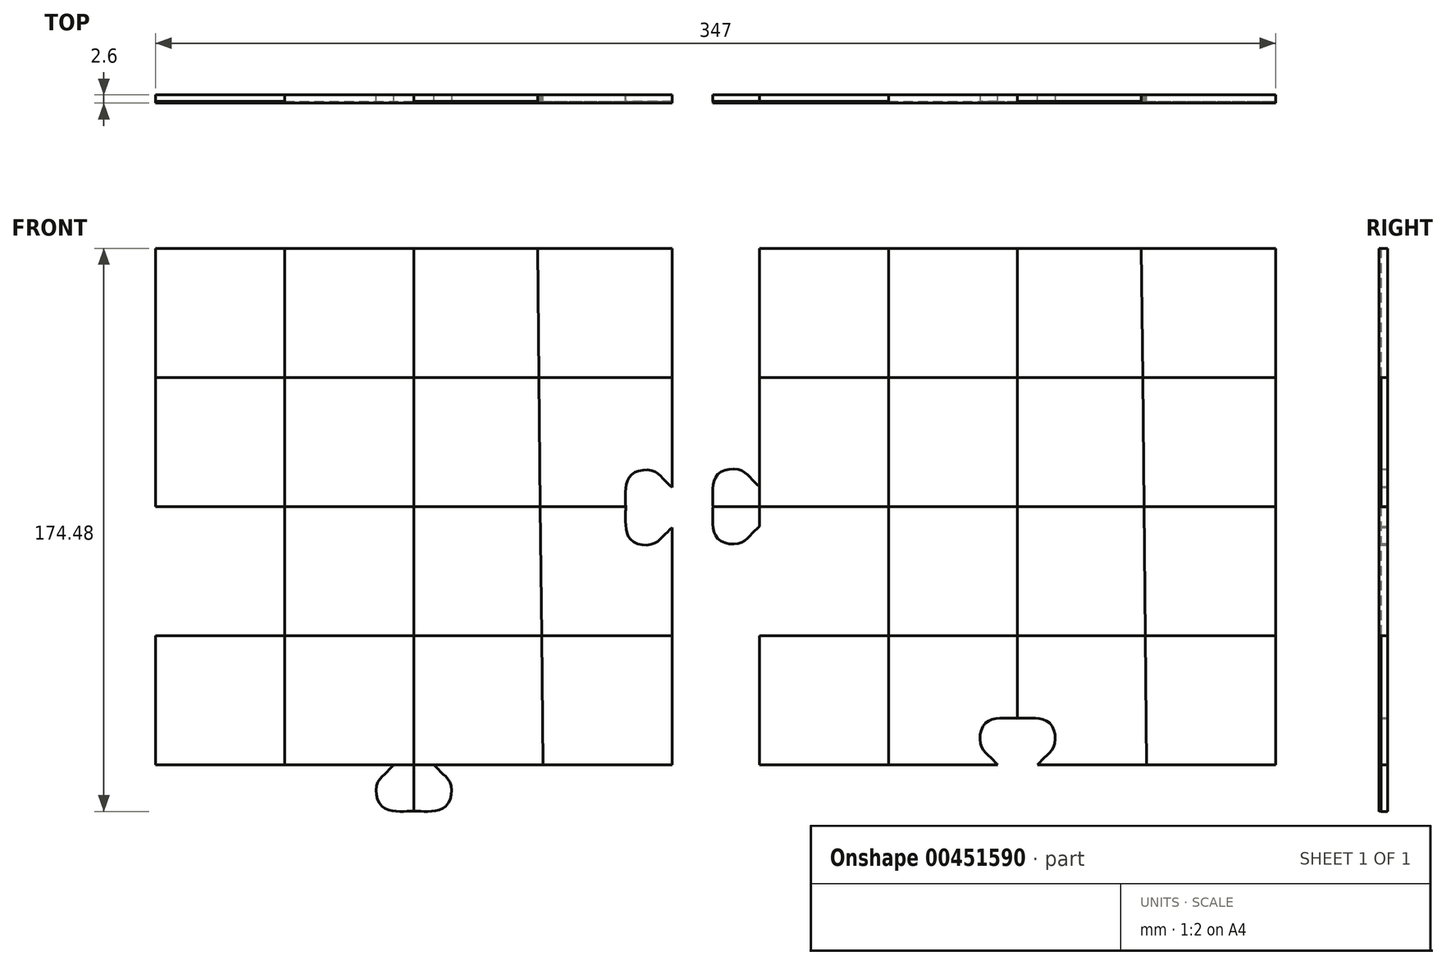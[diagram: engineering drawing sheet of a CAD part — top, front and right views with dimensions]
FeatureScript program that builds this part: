
annotation { "Feature Type Name" : "Feature", "Feature Type Description" : "" }
export const myFeature = defineFeature(function(context is Context, id is Id, definition is map)
    precondition{}
    {
        {
            var Q0;
            Q0=qCreatedBy(makeId("Front.planeOp"),FACE);
            var sketch = newSketch(context, id + "F0", { "sketchPlane" : qUnion([Q0])});
            skLineSegment(sketch, "E0.bottom", {"start": v(-114.43, 88.84) * mm, "end": v(45.57, 88.84) * mm});
            skLineSegment(sketch, "E0.top", {"start": v(-114.43, -71.16) * mm, "end": v(45.57, -71.16) * mm});
            skLineSegment(sketch, "E0.left", {"start": v(-114.43, 88.84) * mm, "end": v(-114.43, -71.16) * mm});
            skLineSegment(sketch, "E0.right", {"start": v(45.57, 88.84) * mm, "end": v(45.57, -71.16) * mm});
            skLineSegment(sketch, "E1", {"start": v(-34.43, 88.84) * mm, "end": v(-34.43, -71.16) * mm});
            skLineSegment(sketch, "E2", {"start": v(-74.43, 88.84) * mm, "end": v(-74.43, -71.16) * mm});
            skLineSegment(sketch, "E3", {"start": v(3.9, 88.84) * mm, "end": v(5.57, -71.16) * mm});
            skLineSegment(sketch, "E4", {"start": v(-114.43, 8.84) * mm, "end": v(45.57, 8.84) * mm});
            skLineSegment(sketch, "E5", {"start": v(-114.43, 48.84) * mm, "end": v(45.57, 48.84) * mm});
            skLineSegment(sketch, "E6", {"start": v(-114.43, 8.84) * mm, "end": v(-114.43, -31.16) * mm});
            skLineSegment(sketch, "E7", {"start": v(-114.43, -31.16) * mm, "end": v(45.57, -31.16) * mm});
            skFitSpline(sketch, "E8", {"points": [v(-114.43, 2.66) * mm, v(-117.14, 0) * mm, v(-120.5, -2.53) * mm, v(-126.7, -1.62) * mm, v(-128.78, 2.84) * mm, v(-128.87, 7.11) * mm, v(-128.78, 8.84) * mm], "startDerivative": vector(-16.05, -15.15) * mm, "endDerivative": vector(1.61, 12.92) * mm});
            skFitSpline(sketch, "E9.MirrorCS", {"points": [v(-114.43, 15.03) * mm, v(-117.14, 17.69) * mm, v(-120.5, 20.22) * mm, v(-126.7, 19.3) * mm, v(-128.78, 14.85) * mm, v(-128.87, 10.57) * mm, v(-128.78, 8.84) * mm], "startDerivative": vector(-16.05, 15.15) * mm, "endDerivative": vector(1.61, -12.92) * mm});
            skLineSegment(sketch, "E10.bottom", {"start": v(-301.43, 88.84) * mm, "end": v(-141.43, 88.84) * mm});
            skLineSegment(sketch, "E10.top", {"start": v(-301.43, -71.16) * mm, "end": v(-141.43, -71.16) * mm});
            skLineSegment(sketch, "E10.left", {"start": v(-301.43, 88.84) * mm, "end": v(-301.43, -71.16) * mm});
            skLineSegment(sketch, "E10.right", {"start": v(-141.43, 88.84) * mm, "end": v(-141.43, -71.16) * mm});
            skLineSegment(sketch, "E11", {"start": v(-221.43, 88.84) * mm, "end": v(-221.43, -71.16) * mm});
            skLineSegment(sketch, "E12", {"start": v(-261.43, 88.84) * mm, "end": v(-261.43, -71.16) * mm});
            skLineSegment(sketch, "E13", {"start": v(-183.1, 88.84) * mm, "end": v(-181.43, -71.16) * mm});
            skLineSegment(sketch, "E14", {"start": v(-301.43, 8.84) * mm, "end": v(-141.43, 8.84) * mm});
            skLineSegment(sketch, "E15", {"start": v(-301.43, 48.84) * mm, "end": v(-141.43, 48.84) * mm});
            skLineSegment(sketch, "E16", {"start": v(-301.43, 8.84) * mm, "end": v(-301.43, -31.16) * mm});
            skLineSegment(sketch, "E17", {"start": v(-301.43, -31.16) * mm, "end": v(-141.43, -31.16) * mm});
            skFitSpline(sketch, "E18", {"points": [v(-141.43, 2.37) * mm, v(-144.14, -0.29) * mm, v(-147.5, -2.82) * mm, v(-153.7, -1.9) * mm, v(-155.78, 2.55) * mm, v(-155.87, 6.83) * mm, v(-155.78, 8.56) * mm], "startDerivative": vector(-16.05, -15.15) * mm, "endDerivative": vector(1.61, 12.92) * mm});
            skFitSpline(sketch, "E19.MirrorCS", {"points": [v(-141.43, 14.74) * mm, v(-144.14, 17.4) * mm, v(-147.5, 19.93) * mm, v(-153.7, 19.02) * mm, v(-155.78, 14.56) * mm, v(-155.87, 10.29) * mm, v(-155.78, 8.56) * mm], "startDerivative": vector(-16.05, 15.15) * mm, "endDerivative": vector(1.61, -12.92) * mm});
            skFitSpline(sketch, "E20.MirrorCS", {"points": [v(-227.62, -71.16) * mm, v(-230.27, -73.86) * mm, v(-232.8, -77.23) * mm, v(-231.9, -83.42) * mm, v(-227.44, -85.51) * mm, v(-223.16, -85.6) * mm, v(-221.43, -85.51) * mm], "startDerivative": vector(-15.15, -16.05) * mm, "endDerivative": vector(12.92, 1.61) * mm});
            skFitSpline(sketch, "E21.MirrorCS", {"points": [v(-215.24, -71.16) * mm, v(-212.59, -73.86) * mm, v(-210.05, -77.23) * mm, v(-210.96, -83.42) * mm, v(-215.42, -85.51) * mm, v(-219.7, -85.6) * mm, v(-221.43, -85.51) * mm], "startDerivative": vector(15.15, -16.05) * mm, "endDerivative": vector(-12.92, 1.61) * mm});
            skLineSegment(sketch, "E22", {"start": v(-114.43, 8.84) * mm, "end": v(-128.78, 8.84) * mm});
            skFitSpline(sketch, "E23.MirrorCS", {"points": [v(-28.24, -71.16) * mm, v(-25.59, -68.45) * mm, v(-23.05, -65.08) * mm, v(-23.96, -58.9) * mm, v(-28.42, -56.8) * mm, v(-32.7, -56.71) * mm, v(-34.43, -56.8) * mm], "startDerivative": vector(15.15, 16.05) * mm, "endDerivative": vector(-12.92, -1.61) * mm});
            skFitSpline(sketch, "E24.MirrorCS", {"points": [v(-40.62, -71.16) * mm, v(-43.27, -68.45) * mm, v(-45.8, -65.08) * mm, v(-44.9, -58.9) * mm, v(-40.44, -56.8) * mm, v(-36.16, -56.71) * mm, v(-34.43, -56.8) * mm], "startDerivative": vector(-15.15, 16.05) * mm, "endDerivative": vector(12.92, -1.61) * mm});
            skLineSegment(sketch, "E25", {"start": v(-221.43, -71.16) * mm, "end": v(-221.43, -85.51) * mm});
            skSolve(sketch);
        }
        {
            var Q0;
            {var subQ0=sQuery(id+"F0.wireOp",EDGE,"E0.left");var subQ1=sQuery(id+"F0.wireOp",EDGE,"E0.bottom");var subQ2=makeQuery(id+"F0.imprint","INTERSECT",VERTEX,{"derivedFrom":[subQ1,subQ0]});Q0=makeQuery(id+"F0.imprint","IMPRINT",FACE,{"disambiguationData":[TD([[makeQuery(id+"F0.imprint","IMPRINT",EDGE,{"disambiguationData":[TD([[subQ2,-1.0]])],"derivedFrom":subQ1}),-1.0]])]});}
            var Q1;
            {var subQ0=sQuery(id+"F0.wireOp",EDGE,"E1");var subQ1=sQuery(id+"F0.wireOp",EDGE,"E0.bottom");var subQ2=makeQuery(id+"F0.imprint","INTERSECT",VERTEX,{"derivedFrom":[subQ1,subQ0]});Q1=makeQuery(id+"F0.imprint","IMPRINT",FACE,{"disambiguationData":[TD([[makeQuery(id+"F0.imprint","IMPRINT",EDGE,{"disambiguationData":[TD([[subQ2,-1.0]])],"derivedFrom":subQ1}),-1.0]])]});}
            var Q2;
            {var subQ0=sQuery(id+"F0.wireOp",EDGE,"E5");var subQ1=sQuery(id+"F0.wireOp",EDGE,"E1");var subQ2=makeQuery(id+"F0.imprint","INTERSECT",VERTEX,{"derivedFrom":[subQ1,subQ0]});Q2=makeQuery(id+"F0.imprint","IMPRINT",FACE,{"disambiguationData":[TD([[makeQuery(id+"F0.imprint","IMPRINT",EDGE,{"disambiguationData":[TD([[subQ2,-1.0]])],"derivedFrom":subQ1}),-1.0]])]});}
            var Q3;
            {var subQ0=sQuery(id+"F0.wireOp",EDGE,"E4");var subQ1=sQuery(id+"F0.wireOp",EDGE,"E0.right");var subQ2=makeQuery(id+"F0.imprint","INTERSECT",VERTEX,{"derivedFrom":[subQ1,subQ0]});Q3=makeQuery(id+"F0.imprint","IMPRINT",FACE,{"disambiguationData":[TD([[makeQuery(id+"F0.imprint","IMPRINT",EDGE,{"disambiguationData":[TD([[subQ2,1.0]])],"derivedFrom":subQ1}),-1.0]])]});}
            var Q4;
            {var subQ5=sQuery(id+"F0.wireOp",EDGE,"E6");Q4=makeQuery(id+"F0.imprint","IMPRINT",FACE,{"disambiguationData":[TD([[makeQuery(id+"F0.imprint","IMPRINT",EDGE,{"derivedFrom":subQ5}),1.0]])]});}
            var Q5;
            {var subQ0=sQuery(id+"F0.wireOp",EDGE,"E4");var subQ1=sQuery(id+"F0.wireOp",EDGE,"E1");var subQ2=makeQuery(id+"F0.imprint","INTERSECT",VERTEX,{"derivedFrom":[subQ1,subQ0]});Q5=makeQuery(id+"F0.imprint","IMPRINT",FACE,{"disambiguationData":[TD([[makeQuery(id+"F0.imprint","IMPRINT",EDGE,{"disambiguationData":[TD([[subQ2,-1.0]])],"derivedFrom":subQ1}),1.0]])]});}
            var Q6;
            {var subQ0=sQuery(id+"F0.wireOp",EDGE,"E1");var subQ1=sQuery(id+"F0.wireOp",EDGE,"E0.top");var subQ2=makeQuery(id+"F0.imprint","INTERSECT",VERTEX,{"derivedFrom":[subQ1,subQ0]});Q6=makeQuery(id+"F0.imprint","IMPRINT",FACE,{"disambiguationData":[TD([[makeQuery(id+"F0.imprint","IMPRINT",EDGE,{"disambiguationData":[TD([[subQ2,1.0]])],"derivedFrom":subQ1}),1.0]])]});}
            var Q7;
            {var subQ0=sQuery(id+"F0.wireOp",EDGE,"E0.right");var subQ1=sQuery(id+"F0.wireOp",EDGE,"E0.top");var subQ2=makeQuery(id+"F0.imprint","INTERSECT",VERTEX,{"derivedFrom":[subQ1,subQ0]});Q7=makeQuery(id+"F0.imprint","IMPRINT",FACE,{"disambiguationData":[TD([[makeQuery(id+"F0.imprint","IMPRINT",EDGE,{"disambiguationData":[TD([[subQ2,1.0]])],"derivedFrom":subQ1}),1.0]])]});}
            var Q8;
            {var subQ7=sQuery(id+"F0.wireOp",EDGE,"E24.MirrorCS");Q8=makeQuery(id+"F0.imprint","IMPRINT",FACE,{"disambiguationData":[TD([[makeQuery(id+"F0.imprint","IMPRINT",EDGE,{"derivedFrom":subQ7}),1.0]])]});}
            extrude(context, id + "F1", {"entities" : qUnion([Q0, Q1, Q2, Q3, Q4, Q5, Q6, Q7, Q8]), "depth" : 2 * mm});
        }
        {
            var Q0;
            {var subQ0=sQuery(id+"F0.wireOp",EDGE,"E1");var subQ1=sQuery(id+"F0.wireOp",EDGE,"E0.bottom");var subQ2=makeQuery(id+"F0.imprint","INTERSECT",VERTEX,{"derivedFrom":[subQ1,subQ0]});Q0=makeQuery(id+"F0.imprint","IMPRINT",FACE,{"disambiguationData":[TD([[makeQuery(id+"F0.imprint","IMPRINT",EDGE,{"disambiguationData":[TD([[subQ2,1.0]])],"derivedFrom":subQ1}),-1.0]])]});}
            var Q1;
            {var subQ0=sQuery(id+"F0.wireOp",EDGE,"E0.right");var subQ1=sQuery(id+"F0.wireOp",EDGE,"E0.bottom");var subQ2=makeQuery(id+"F0.imprint","INTERSECT",VERTEX,{"derivedFrom":[subQ1,subQ0]});Q1=makeQuery(id+"F0.imprint","IMPRINT",FACE,{"disambiguationData":[TD([[makeQuery(id+"F0.imprint","IMPRINT",EDGE,{"disambiguationData":[TD([[subQ2,1.0]])],"derivedFrom":subQ1}),-1.0]])]});}
            var Q2;
            {var subQ0=sQuery(id+"F0.wireOp",EDGE,"E5");var subQ1=sQuery(id+"F0.wireOp",EDGE,"E1");var subQ2=makeQuery(id+"F0.imprint","INTERSECT",VERTEX,{"derivedFrom":[subQ1,subQ0]});Q2=makeQuery(id+"F0.imprint","IMPRINT",FACE,{"disambiguationData":[TD([[makeQuery(id+"F0.imprint","IMPRINT",EDGE,{"disambiguationData":[TD([[subQ2,-1.0]])],"derivedFrom":subQ1}),1.0]])]});}
            var Q3;
            {var subQ3=sQuery(id+"F0.wireOp",EDGE,"E5");var subQ5=sQuery(id+"F0.wireOp",EDGE,"E2");var subQ6=makeQuery(id+"F0.imprint","INTERSECT",VERTEX,{"derivedFrom":[subQ5,subQ3]});Q3=makeQuery(id+"F0.imprint","IMPRINT",FACE,{"disambiguationData":[TD([[makeQuery(id+"F0.imprint","IMPRINT",EDGE,{"disambiguationData":[TD([[subQ6,-1.0]])],"derivedFrom":subQ5}),-1.0]])]});}
            var Q4;
            {var subQ0=sQuery(id+"F0.wireOp",EDGE,"E4");var subQ1=sQuery(id+"F0.wireOp",EDGE,"E1");var subQ2=makeQuery(id+"F0.imprint","INTERSECT",VERTEX,{"derivedFrom":[subQ1,subQ0]});Q4=makeQuery(id+"F0.imprint","IMPRINT",FACE,{"disambiguationData":[TD([[makeQuery(id+"F0.imprint","IMPRINT",EDGE,{"disambiguationData":[TD([[subQ2,-1.0]])],"derivedFrom":subQ1}),-1.0]])]});}
            var Q5;
            {var subQ0=sQuery(id+"F0.wireOp",EDGE,"E4");var subQ1=sQuery(id+"F0.wireOp",EDGE,"E0.right");var subQ2=makeQuery(id+"F0.imprint","INTERSECT",VERTEX,{"derivedFrom":[subQ1,subQ0]});Q5=makeQuery(id+"F0.imprint","IMPRINT",FACE,{"disambiguationData":[TD([[makeQuery(id+"F0.imprint","IMPRINT",EDGE,{"disambiguationData":[TD([[subQ2,-1.0]])],"derivedFrom":subQ1}),-1.0]])]});}
            var Q6;
            {var subQ0=sQuery(id+"F0.wireOp",EDGE,"E0.left");var subQ1=sQuery(id+"F0.wireOp",EDGE,"E0.top");var subQ2=makeQuery(id+"F0.imprint","INTERSECT",VERTEX,{"derivedFrom":[subQ1,subQ0]});Q6=makeQuery(id+"F0.imprint","IMPRINT",FACE,{"disambiguationData":[TD([[makeQuery(id+"F0.imprint","IMPRINT",EDGE,{"disambiguationData":[TD([[subQ2,-1.0]])],"derivedFrom":subQ1}),1.0]])]});}
            var Q7;
            {var subQ0=sQuery(id+"F0.wireOp",EDGE,"E1");var subQ1=sQuery(id+"F0.wireOp",EDGE,"E0.top");var subQ2=makeQuery(id+"F0.imprint","INTERSECT",VERTEX,{"derivedFrom":[subQ1,subQ0]});Q7=makeQuery(id+"F0.imprint","IMPRINT",FACE,{"disambiguationData":[TD([[makeQuery(id+"F0.imprint","IMPRINT",EDGE,{"disambiguationData":[TD([[subQ2,-1.0]])],"derivedFrom":subQ1}),1.0]])]});}
            var Q8;
            {var subQ5=sQuery(id+"F0.wireOp",EDGE,"E23.MirrorCS");Q8=makeQuery(id+"F0.imprint","IMPRINT",FACE,{"disambiguationData":[TD([[makeQuery(id+"F0.imprint","IMPRINT",EDGE,{"derivedFrom":subQ5}),-1.0]])]});}
            extrude(context, id + "F2", {"entities" : qUnion([Q0, Q1, Q2, Q3, Q4, Q5, Q6, Q7, Q8]), "depth" : 2.6 * mm});
        }
        {
            var Q0;
            {var subQ3=sQuery(id+"F0.wireOp",EDGE,"E9.MirrorCS");Q0=makeQuery(id+"F0.imprint","IMPRINT",FACE,{"disambiguationData":[TD([[makeQuery(id+"F0.imprint","IMPRINT",EDGE,{"derivedFrom":subQ3}),1.0]])]});}
            extrude(context, id + "F3", {"entities" : qUnion([Q0]), "operationType" : NewBodyOperationType.ADD, "depth" : 2 * mm});
        }
        {
            var Q0;
            {var subQ3=sQuery(id+"F0.wireOp",EDGE,"E8");Q0=makeQuery(id+"F0.imprint","IMPRINT",FACE,{"disambiguationData":[TD([[makeQuery(id+"F0.imprint","IMPRINT",EDGE,{"derivedFrom":subQ3}),-1.0]])]});}
            extrude(context, id + "F4", {"entities" : qUnion([Q0]), "depth" : 2.6 * mm});
        }
        {
            var Q0;
            {var subQ0=sQuery(id+"F0.wireOp",EDGE,"E10.right");var subQ1=sQuery(id+"F0.wireOp",EDGE,"E10.bottom");var subQ2=makeQuery(id+"F0.imprint","INTERSECT",VERTEX,{"derivedFrom":[subQ1,subQ0]});Q0=makeQuery(id+"F0.imprint","IMPRINT",FACE,{"disambiguationData":[TD([[makeQuery(id+"F0.imprint","IMPRINT",EDGE,{"disambiguationData":[TD([[subQ2,1.0]])],"derivedFrom":subQ1}),-1.0]])]});}
            var Q1;
            {var subQ0=sQuery(id+"F0.wireOp",EDGE,"E11");var subQ1=sQuery(id+"F0.wireOp",EDGE,"E10.bottom");var subQ2=makeQuery(id+"F0.imprint","INTERSECT",VERTEX,{"derivedFrom":[subQ1,subQ0]});Q1=makeQuery(id+"F0.imprint","IMPRINT",FACE,{"disambiguationData":[TD([[makeQuery(id+"F0.imprint","IMPRINT",EDGE,{"disambiguationData":[TD([[subQ2,1.0]])],"derivedFrom":subQ1}),-1.0]])]});}
            var Q2;
            {var subQ3=sQuery(id+"F0.wireOp",EDGE,"E15");var subQ5=sQuery(id+"F0.wireOp",EDGE,"E12");var subQ7=makeQuery(id+"F0.imprint","INTERSECT",VERTEX,{"derivedFrom":[subQ5,subQ3]});Q2=makeQuery(id+"F0.imprint","IMPRINT",FACE,{"disambiguationData":[TD([[makeQuery(id+"F0.imprint","IMPRINT",EDGE,{"disambiguationData":[TD([[subQ7,-1.0]])],"derivedFrom":subQ5}),-1.0]])]});}
            var Q3;
            {var subQ0=sQuery(id+"F0.wireOp",EDGE,"E15");var subQ1=sQuery(id+"F0.wireOp",EDGE,"E11");var subQ2=makeQuery(id+"F0.imprint","INTERSECT",VERTEX,{"derivedFrom":[subQ1,subQ0]});Q3=makeQuery(id+"F0.imprint","IMPRINT",FACE,{"disambiguationData":[TD([[makeQuery(id+"F0.imprint","IMPRINT",EDGE,{"disambiguationData":[TD([[subQ2,-1.0]])],"derivedFrom":subQ1}),1.0]])]});}
            var Q4;
            {var subQ0=sQuery(id+"F0.wireOp",EDGE,"E14");var subQ1=sQuery(id+"F0.wireOp",EDGE,"E11");var subQ2=makeQuery(id+"F0.imprint","INTERSECT",VERTEX,{"derivedFrom":[subQ1,subQ0]});Q4=makeQuery(id+"F0.imprint","IMPRINT",FACE,{"disambiguationData":[TD([[makeQuery(id+"F0.imprint","IMPRINT",EDGE,{"disambiguationData":[TD([[subQ2,-1.0]])],"derivedFrom":subQ1}),-1.0]])]});}
            var Q5;
            {var subQ9=sQuery(id+"F0.wireOp",EDGE,"E18");Q5=makeQuery(id+"F0.imprint","IMPRINT",FACE,{"disambiguationData":[TD([[makeQuery(id+"F0.imprint","IMPRINT",EDGE,{"derivedFrom":subQ9}),1.0]])]});}
            var Q6;
            {var subQ0=sQuery(id+"F0.wireOp",EDGE,"E10.left");var subQ1=sQuery(id+"F0.wireOp",EDGE,"E10.top");var subQ2=makeQuery(id+"F0.imprint","INTERSECT",VERTEX,{"derivedFrom":[subQ1,subQ0]});Q6=makeQuery(id+"F0.imprint","IMPRINT",FACE,{"disambiguationData":[TD([[makeQuery(id+"F0.imprint","IMPRINT",EDGE,{"disambiguationData":[TD([[subQ2,-1.0]])],"derivedFrom":subQ1}),1.0]])]});}
            var Q7;
            {var subQ0=sQuery(id+"F0.wireOp",EDGE,"E11");var subQ1=sQuery(id+"F0.wireOp",EDGE,"E10.top");var subQ2=makeQuery(id+"F0.imprint","INTERSECT",VERTEX,{"derivedFrom":[subQ1,subQ0]});Q7=makeQuery(id+"F0.imprint","IMPRINT",FACE,{"disambiguationData":[TD([[makeQuery(id+"F0.imprint","IMPRINT",EDGE,{"disambiguationData":[TD([[subQ2,-1.0]])],"derivedFrom":subQ1}),1.0]])]});}
            extrude(context, id + "F5", {"entities" : qUnion([Q0, Q1, Q2, Q3, Q4, Q5, Q6, Q7]), "depth" : 2.6 * mm});
        }
        {
            var Q0;
            {var subQ0=sQuery(id+"F0.wireOp",EDGE,"E10.left");var subQ1=sQuery(id+"F0.wireOp",EDGE,"E10.bottom");var subQ2=makeQuery(id+"F0.imprint","INTERSECT",VERTEX,{"derivedFrom":[subQ1,subQ0]});Q0=makeQuery(id+"F0.imprint","IMPRINT",FACE,{"disambiguationData":[TD([[makeQuery(id+"F0.imprint","IMPRINT",EDGE,{"disambiguationData":[TD([[subQ2,-1.0]])],"derivedFrom":subQ1}),-1.0]])]});}
            var Q1;
            {var subQ0=sQuery(id+"F0.wireOp",EDGE,"E11");var subQ1=sQuery(id+"F0.wireOp",EDGE,"E10.bottom");var subQ2=makeQuery(id+"F0.imprint","INTERSECT",VERTEX,{"derivedFrom":[subQ1,subQ0]});Q1=makeQuery(id+"F0.imprint","IMPRINT",FACE,{"disambiguationData":[TD([[makeQuery(id+"F0.imprint","IMPRINT",EDGE,{"disambiguationData":[TD([[subQ2,-1.0]])],"derivedFrom":subQ1}),-1.0]])]});}
            var Q2;
            {var subQ0=sQuery(id+"F0.wireOp",EDGE,"E15");var subQ1=sQuery(id+"F0.wireOp",EDGE,"E11");var subQ2=makeQuery(id+"F0.imprint","INTERSECT",VERTEX,{"derivedFrom":[subQ1,subQ0]});Q2=makeQuery(id+"F0.imprint","IMPRINT",FACE,{"disambiguationData":[TD([[makeQuery(id+"F0.imprint","IMPRINT",EDGE,{"disambiguationData":[TD([[subQ2,-1.0]])],"derivedFrom":subQ1}),-1.0]])]});}
            var Q3;
            {var subQ0=sQuery(id+"F0.wireOp",EDGE,"E15");var subQ1=sQuery(id+"F0.wireOp",EDGE,"E10.right");var subQ2=makeQuery(id+"F0.imprint","INTERSECT",VERTEX,{"derivedFrom":[subQ1,subQ0]});Q3=makeQuery(id+"F0.imprint","IMPRINT",FACE,{"disambiguationData":[TD([[makeQuery(id+"F0.imprint","IMPRINT",EDGE,{"disambiguationData":[TD([[subQ2,-1.0]])],"derivedFrom":subQ1}),-1.0]])]});}
            var Q4;
            {var subQ0=sQuery(id+"F0.wireOp",EDGE,"E14");var subQ1=sQuery(id+"F0.wireOp",EDGE,"E11");var subQ2=makeQuery(id+"F0.imprint","INTERSECT",VERTEX,{"derivedFrom":[subQ1,subQ0]});Q4=makeQuery(id+"F0.imprint","IMPRINT",FACE,{"disambiguationData":[TD([[makeQuery(id+"F0.imprint","IMPRINT",EDGE,{"disambiguationData":[TD([[subQ2,-1.0]])],"derivedFrom":subQ1}),1.0]])]});}
            var Q5;
            {var subQ5=sQuery(id+"F0.wireOp",EDGE,"E16");Q5=makeQuery(id+"F0.imprint","IMPRINT",FACE,{"disambiguationData":[TD([[makeQuery(id+"F0.imprint","IMPRINT",EDGE,{"derivedFrom":subQ5}),1.0]])]});}
            var Q6;
            {var subQ0=sQuery(id+"F0.wireOp",EDGE,"E11");var subQ1=sQuery(id+"F0.wireOp",EDGE,"E10.top");var subQ2=makeQuery(id+"F0.imprint","INTERSECT",VERTEX,{"derivedFrom":[subQ1,subQ0]});Q6=makeQuery(id+"F0.imprint","IMPRINT",FACE,{"disambiguationData":[TD([[makeQuery(id+"F0.imprint","IMPRINT",EDGE,{"disambiguationData":[TD([[subQ2,1.0]])],"derivedFrom":subQ1}),1.0]])]});}
            var Q7;
            {var subQ0=sQuery(id+"F0.wireOp",EDGE,"E10.right");var subQ1=sQuery(id+"F0.wireOp",EDGE,"E10.top");var subQ2=makeQuery(id+"F0.imprint","INTERSECT",VERTEX,{"derivedFrom":[subQ1,subQ0]});Q7=makeQuery(id+"F0.imprint","IMPRINT",FACE,{"disambiguationData":[TD([[makeQuery(id+"F0.imprint","IMPRINT",EDGE,{"disambiguationData":[TD([[subQ2,1.0]])],"derivedFrom":subQ1}),1.0]])]});}
            extrude(context, id + "F6", {"entities" : qUnion([Q0, Q1, Q2, Q3, Q4, Q5, Q6, Q7]), "depth" : 2 * mm});
        }
        {
            var Q0;
            {var subQ3=sQuery(id+"F0.wireOp",EDGE,"E21.MirrorCS");Q0=makeQuery(id+"F0.imprint","IMPRINT",FACE,{"disambiguationData":[TD([[makeQuery(id+"F0.imprint","IMPRINT",EDGE,{"derivedFrom":subQ3}),-1.0]])]});}
            extrude(context, id + "F7", {"entities" : qUnion([Q0]), "operationType" : NewBodyOperationType.ADD, "depth" : 2 * mm});
        }
        {
            var Q0;
            {var subQ3=sQuery(id+"F0.wireOp",EDGE,"E20.MirrorCS");Q0=makeQuery(id+"F0.imprint","IMPRINT",FACE,{"disambiguationData":[TD([[makeQuery(id+"F0.imprint","IMPRINT",EDGE,{"derivedFrom":subQ3}),1.0]])]});}
            extrude(context, id + "F8", {"entities" : qUnion([Q0]), "depth" : 2.6 * mm});
        }
        {
            var Q0;
            {var subQ3=sQuery(id+"F0.wireOp",EDGE,"E23.MirrorCS");Q0=makeQuery(id+"F0.imprint","IMPRINT",FACE,{"disambiguationData":[TD([[makeQuery(id+"F0.imprint","IMPRINT",EDGE,{"derivedFrom":subQ3}),1.0]])]});}
            var Q1;
            {var subQ3=sQuery(id+"F0.wireOp",EDGE,"E24.MirrorCS");Q1=makeQuery(id+"F0.imprint","IMPRINT",FACE,{"disambiguationData":[TD([[makeQuery(id+"F0.imprint","IMPRINT",EDGE,{"derivedFrom":subQ3}),-1.0]])]});}
            extrude(context, id + "F9", {"entities" : qUnion([Q0, Q1]), "operationType" : NewBodyOperationType.REMOVE, "endBound" : BoundingType.SYMMETRIC, "depth" : 17 * mm, "offsetDistance" : 25 * mm});
        }
        {
            var Q0;
            {var subQ3=sQuery(id+"F0.wireOp",EDGE,"E24.MirrorCS");Q0=makeQuery(id+"F0.imprint","IMPRINT",FACE,{"disambiguationData":[TD([[makeQuery(id+"F0.imprint","IMPRINT",EDGE,{"derivedFrom":subQ3}),-1.0]])]});}
            var Q1;
            {var subQ3=sQuery(id+"F0.wireOp",EDGE,"E23.MirrorCS");Q1=makeQuery(id+"F0.imprint","IMPRINT",FACE,{"disambiguationData":[TD([[makeQuery(id+"F0.imprint","IMPRINT",EDGE,{"derivedFrom":subQ3}),1.0]])]});}
            extrude(context, id + "F10", {"entities" : qUnion([Q0, Q1]), "operationType" : NewBodyOperationType.REMOVE, "endBound" : BoundingType.SYMMETRIC, "oppositeDirection" : true, "depth" : 25 * mm});
        }
    });
